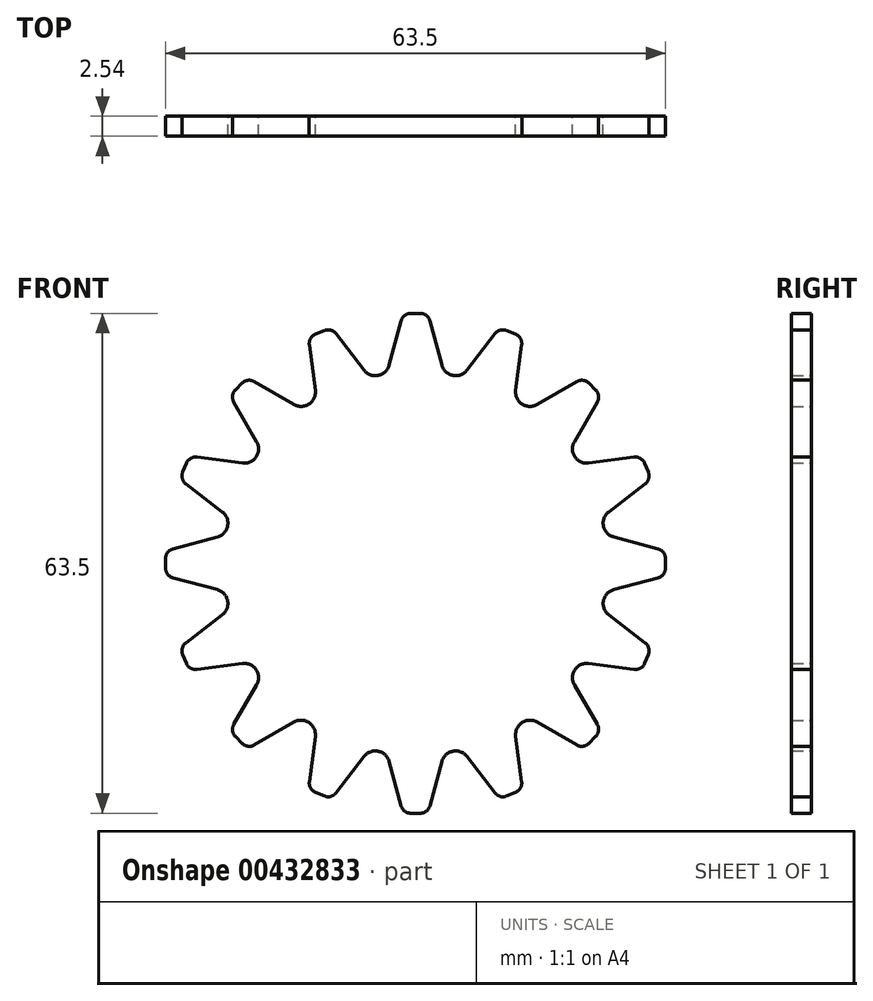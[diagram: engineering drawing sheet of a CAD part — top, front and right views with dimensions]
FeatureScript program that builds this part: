
annotation { "Feature Type Name" : "Feature", "Feature Type Description" : "" }
export const myFeature = defineFeature(function(context is Context, id is Id, definition is map)
    precondition{}
    {
        {
            var Q0;
            Q0=qCreatedBy(makeId("Front.planeOp"),FACE);
            var sketch = newSketch(context, id + "F0", { "sketchPlane" : qUnion([Q0])});
            skCircle(sketch, "E0", {"center": v(0, 0) * mm, "radius": 25.4 * mm, "construction": true});
            skPoint(sketch, "E1", {"position": v(0, 31.75) * mm});
            skLineSegment(sketch, "E2", {"start": v(-0.61, 31.75) * mm, "end": v(0.61, 31.75) * mm});
            skLineSegment(sketch, "E3", {"start": v(-1.84, 30.8) * mm, "end": v(-3.35, 25.18) * mm});
            skLineSegment(sketch, "E4.MirrorCS", {"start": v(1.84, 30.8) * mm, "end": v(3.35, 25.18) * mm});
            skPoint(sketch, "E5.visualSharp", {"position": v(-1.59, 31.75) * mm});
            skArc(sketch, "E5.filletArc", {"start": v(-0.61, 31.75) * mm, "mid": v(-1.39, 31.49) * mm, "end": v(-1.84, 30.8) * mm});
            skArc(sketch, "E6.MirrorCS", {"start": v(0.61, 31.75) * mm, "mid": v(1.39, 31.49) * mm, "end": v(1.84, 30.8) * mm});
            skPoint(sketch, "E7.orphan", {"position": v(1.59, 31.75) * mm});
            skArc(sketch, "E8", {"start": v(3.35, 25.18) * mm, "mid": v(4.75, 23.87) * mm, "end": v(6.54, 24.54) * mm});
            skLineSegment(sketch, "E9.1.0", {"start": v(-13.49, 27.76) * mm, "end": v(-12.73, 21.98) * mm});
            skArc(sketch, "E9.1.1", {"start": v(-12.72, 29.1) * mm, "mid": v(-13.33, 28.56) * mm, "end": v(-13.49, 27.76) * mm});
            skLineSegment(sketch, "E9.1.2", {"start": v(-12.72, 29.1) * mm, "end": v(-11.58, 29.57) * mm});
            skArc(sketch, "E9.1.3", {"start": v(-11.58, 29.57) * mm, "mid": v(-10.77, 29.62) * mm, "end": v(-10.1, 29.17) * mm});
            skLineSegment(sketch, "E9.1.4", {"start": v(-10.1, 29.17) * mm, "end": v(-6.54, 24.54) * mm});
            skArc(sketch, "E9.1.5", {"start": v(-6.54, 24.54) * mm, "mid": v(-4.75, 23.87) * mm, "end": v(-3.35, 25.18) * mm});
            skLineSegment(sketch, "E9.2.0", {"start": v(-23.09, 20.48) * mm, "end": v(-20.17, 15.44) * mm});
            skArc(sketch, "E9.2.1", {"start": v(-22.88, 22.02) * mm, "mid": v(-23.25, 21.28) * mm, "end": v(-23.09, 20.48) * mm});
            skLineSegment(sketch, "E9.2.2", {"start": v(-22.88, 22.02) * mm, "end": v(-22.02, 22.88) * mm});
            skArc(sketch, "E9.2.3", {"start": v(-22.02, 22.88) * mm, "mid": v(-21.28, 23.25) * mm, "end": v(-20.48, 23.09) * mm});
            skLineSegment(sketch, "E9.2.4", {"start": v(-20.48, 23.09) * mm, "end": v(-15.44, 20.17) * mm});
            skArc(sketch, "E9.2.5", {"start": v(-15.44, 20.17) * mm, "mid": v(-13.52, 20.23) * mm, "end": v(-12.73, 21.98) * mm});
            skLineSegment(sketch, "E9.3.0", {"start": v(-29.17, 10.1) * mm, "end": v(-24.54, 6.54) * mm});
            skArc(sketch, "E9.3.1", {"start": v(-29.57, 11.58) * mm, "mid": v(-29.62, 10.77) * mm, "end": v(-29.17, 10.1) * mm});
            skLineSegment(sketch, "E9.3.2", {"start": v(-29.57, 11.58) * mm, "end": v(-29.1, 12.72) * mm});
            skArc(sketch, "E9.3.3", {"start": v(-29.1, 12.72) * mm, "mid": v(-28.56, 13.33) * mm, "end": v(-27.76, 13.49) * mm});
            skLineSegment(sketch, "E9.3.4", {"start": v(-27.76, 13.49) * mm, "end": v(-21.98, 12.73) * mm});
            skArc(sketch, "E9.3.5", {"start": v(-21.98, 12.73) * mm, "mid": v(-20.23, 13.52) * mm, "end": v(-20.17, 15.44) * mm});
            skLineSegment(sketch, "E9.4.0", {"start": v(-30.8, -1.84) * mm, "end": v(-25.18, -3.35) * mm});
            skArc(sketch, "E9.4.1", {"start": v(-31.75, -0.61) * mm, "mid": v(-31.49, -1.39) * mm, "end": v(-30.8, -1.84) * mm});
            skLineSegment(sketch, "E9.4.2", {"start": v(-31.75, -0.61) * mm, "end": v(-31.75, 0.61) * mm});
            skArc(sketch, "E9.4.3", {"start": v(-31.75, 0.61) * mm, "mid": v(-31.49, 1.39) * mm, "end": v(-30.8, 1.84) * mm});
            skLineSegment(sketch, "E9.4.4", {"start": v(-30.8, 1.84) * mm, "end": v(-25.18, 3.35) * mm});
            skArc(sketch, "E9.4.5", {"start": v(-25.18, 3.35) * mm, "mid": v(-23.87, 4.75) * mm, "end": v(-24.54, 6.54) * mm});
            skLineSegment(sketch, "E9.5.0", {"start": v(-27.76, -13.49) * mm, "end": v(-21.98, -12.73) * mm});
            skArc(sketch, "E9.5.1", {"start": v(-29.1, -12.72) * mm, "mid": v(-28.56, -13.33) * mm, "end": v(-27.76, -13.49) * mm});
            skLineSegment(sketch, "E9.5.2", {"start": v(-29.1, -12.72) * mm, "end": v(-29.57, -11.58) * mm});
            skArc(sketch, "E9.5.3", {"start": v(-29.57, -11.58) * mm, "mid": v(-29.62, -10.77) * mm, "end": v(-29.17, -10.1) * mm});
            skLineSegment(sketch, "E9.5.4", {"start": v(-29.17, -10.1) * mm, "end": v(-24.54, -6.54) * mm});
            skArc(sketch, "E9.5.5", {"start": v(-24.54, -6.54) * mm, "mid": v(-23.87, -4.75) * mm, "end": v(-25.18, -3.35) * mm});
            skLineSegment(sketch, "E9.6.0", {"start": v(-20.48, -23.09) * mm, "end": v(-15.44, -20.17) * mm});
            skArc(sketch, "E9.6.1", {"start": v(-22.02, -22.88) * mm, "mid": v(-21.28, -23.25) * mm, "end": v(-20.48, -23.09) * mm});
            skLineSegment(sketch, "E9.6.2", {"start": v(-22.02, -22.88) * mm, "end": v(-22.88, -22.02) * mm});
            skArc(sketch, "E9.6.3", {"start": v(-22.88, -22.02) * mm, "mid": v(-23.25, -21.28) * mm, "end": v(-23.09, -20.48) * mm});
            skLineSegment(sketch, "E9.6.4", {"start": v(-23.09, -20.48) * mm, "end": v(-20.17, -15.44) * mm});
            skArc(sketch, "E9.6.5", {"start": v(-20.17, -15.44) * mm, "mid": v(-20.23, -13.52) * mm, "end": v(-21.98, -12.73) * mm});
            skLineSegment(sketch, "E9.7.0", {"start": v(-10.1, -29.17) * mm, "end": v(-6.54, -24.54) * mm});
            skArc(sketch, "E9.7.1", {"start": v(-11.58, -29.57) * mm, "mid": v(-10.77, -29.62) * mm, "end": v(-10.1, -29.17) * mm});
            skLineSegment(sketch, "E9.7.2", {"start": v(-11.58, -29.57) * mm, "end": v(-12.72, -29.1) * mm});
            skArc(sketch, "E9.7.3", {"start": v(-12.72, -29.1) * mm, "mid": v(-13.33, -28.56) * mm, "end": v(-13.49, -27.76) * mm});
            skLineSegment(sketch, "E9.7.4", {"start": v(-13.49, -27.76) * mm, "end": v(-12.73, -21.98) * mm});
            skArc(sketch, "E9.7.5", {"start": v(-12.73, -21.98) * mm, "mid": v(-13.52, -20.23) * mm, "end": v(-15.44, -20.17) * mm});
            skLineSegment(sketch, "E9.8.0", {"start": v(1.84, -30.8) * mm, "end": v(3.35, -25.18) * mm});
            skArc(sketch, "E9.8.1", {"start": v(0.61, -31.75) * mm, "mid": v(1.39, -31.49) * mm, "end": v(1.84, -30.8) * mm});
            skLineSegment(sketch, "E9.8.2", {"start": v(0.61, -31.75) * mm, "end": v(-0.61, -31.75) * mm});
            skArc(sketch, "E9.8.3", {"start": v(-0.61, -31.75) * mm, "mid": v(-1.39, -31.49) * mm, "end": v(-1.84, -30.8) * mm});
            skLineSegment(sketch, "E9.8.4", {"start": v(-1.84, -30.8) * mm, "end": v(-3.35, -25.18) * mm});
            skArc(sketch, "E9.8.5", {"start": v(-3.35, -25.18) * mm, "mid": v(-4.75, -23.87) * mm, "end": v(-6.54, -24.54) * mm});
            skLineSegment(sketch, "E9.9.0", {"start": v(13.49, -27.76) * mm, "end": v(12.73, -21.98) * mm});
            skArc(sketch, "E9.9.1", {"start": v(12.72, -29.1) * mm, "mid": v(13.33, -28.56) * mm, "end": v(13.49, -27.76) * mm});
            skLineSegment(sketch, "E9.9.2", {"start": v(12.72, -29.1) * mm, "end": v(11.58, -29.57) * mm});
            skArc(sketch, "E9.9.3", {"start": v(11.58, -29.57) * mm, "mid": v(10.77, -29.62) * mm, "end": v(10.1, -29.17) * mm});
            skLineSegment(sketch, "E9.9.4", {"start": v(10.1, -29.17) * mm, "end": v(6.54, -24.54) * mm});
            skArc(sketch, "E9.9.5", {"start": v(6.54, -24.54) * mm, "mid": v(4.75, -23.87) * mm, "end": v(3.35, -25.18) * mm});
            skLineSegment(sketch, "E9.10.0", {"start": v(23.09, -20.48) * mm, "end": v(20.17, -15.44) * mm});
            skArc(sketch, "E9.10.1", {"start": v(22.88, -22.02) * mm, "mid": v(23.25, -21.28) * mm, "end": v(23.09, -20.48) * mm});
            skLineSegment(sketch, "E9.10.2", {"start": v(22.88, -22.02) * mm, "end": v(22.02, -22.88) * mm});
            skArc(sketch, "E9.10.3", {"start": v(22.02, -22.88) * mm, "mid": v(21.28, -23.25) * mm, "end": v(20.48, -23.09) * mm});
            skLineSegment(sketch, "E9.10.4", {"start": v(20.48, -23.09) * mm, "end": v(15.44, -20.17) * mm});
            skArc(sketch, "E9.10.5", {"start": v(15.44, -20.17) * mm, "mid": v(13.52, -20.23) * mm, "end": v(12.73, -21.98) * mm});
            skLineSegment(sketch, "E9.11.0", {"start": v(29.17, -10.1) * mm, "end": v(24.54, -6.54) * mm});
            skArc(sketch, "E9.11.1", {"start": v(29.57, -11.58) * mm, "mid": v(29.62, -10.77) * mm, "end": v(29.17, -10.1) * mm});
            skLineSegment(sketch, "E9.11.2", {"start": v(29.57, -11.58) * mm, "end": v(29.1, -12.72) * mm});
            skArc(sketch, "E9.11.3", {"start": v(29.1, -12.72) * mm, "mid": v(28.56, -13.33) * mm, "end": v(27.76, -13.49) * mm});
            skLineSegment(sketch, "E9.11.4", {"start": v(27.76, -13.49) * mm, "end": v(21.98, -12.73) * mm});
            skArc(sketch, "E9.11.5", {"start": v(21.98, -12.73) * mm, "mid": v(20.23, -13.52) * mm, "end": v(20.17, -15.44) * mm});
            skLineSegment(sketch, "E9.12.0", {"start": v(30.8, 1.84) * mm, "end": v(25.18, 3.35) * mm});
            skArc(sketch, "E9.12.1", {"start": v(31.75, 0.61) * mm, "mid": v(31.49, 1.39) * mm, "end": v(30.8, 1.84) * mm});
            skLineSegment(sketch, "E9.12.2", {"start": v(31.75, 0.61) * mm, "end": v(31.75, -0.61) * mm});
            skArc(sketch, "E9.12.3", {"start": v(31.75, -0.61) * mm, "mid": v(31.49, -1.39) * mm, "end": v(30.8, -1.84) * mm});
            skLineSegment(sketch, "E9.12.4", {"start": v(30.8, -1.84) * mm, "end": v(25.18, -3.35) * mm});
            skArc(sketch, "E9.12.5", {"start": v(25.18, -3.35) * mm, "mid": v(23.87, -4.75) * mm, "end": v(24.54, -6.54) * mm});
            skLineSegment(sketch, "E9.13.0", {"start": v(27.76, 13.49) * mm, "end": v(21.98, 12.73) * mm});
            skArc(sketch, "E9.13.1", {"start": v(29.1, 12.72) * mm, "mid": v(28.56, 13.33) * mm, "end": v(27.76, 13.49) * mm});
            skLineSegment(sketch, "E9.13.2", {"start": v(29.1, 12.72) * mm, "end": v(29.57, 11.58) * mm});
            skArc(sketch, "E9.13.3", {"start": v(29.57, 11.58) * mm, "mid": v(29.62, 10.77) * mm, "end": v(29.17, 10.1) * mm});
            skLineSegment(sketch, "E9.13.4", {"start": v(29.17, 10.1) * mm, "end": v(24.54, 6.54) * mm});
            skArc(sketch, "E9.13.5", {"start": v(24.54, 6.54) * mm, "mid": v(23.87, 4.75) * mm, "end": v(25.18, 3.35) * mm});
            skLineSegment(sketch, "E9.14.0", {"start": v(20.48, 23.09) * mm, "end": v(15.44, 20.17) * mm});
            skArc(sketch, "E9.14.1", {"start": v(22.02, 22.88) * mm, "mid": v(21.28, 23.25) * mm, "end": v(20.48, 23.09) * mm});
            skLineSegment(sketch, "E9.14.2", {"start": v(22.02, 22.88) * mm, "end": v(22.88, 22.02) * mm});
            skArc(sketch, "E9.14.3", {"start": v(22.88, 22.02) * mm, "mid": v(23.25, 21.28) * mm, "end": v(23.09, 20.48) * mm});
            skLineSegment(sketch, "E9.14.4", {"start": v(23.09, 20.48) * mm, "end": v(20.17, 15.44) * mm});
            skArc(sketch, "E9.14.5", {"start": v(20.17, 15.44) * mm, "mid": v(20.23, 13.52) * mm, "end": v(21.98, 12.73) * mm});
            skLineSegment(sketch, "E9.15.0", {"start": v(10.1, 29.17) * mm, "end": v(6.54, 24.54) * mm});
            skArc(sketch, "E9.15.1", {"start": v(11.58, 29.57) * mm, "mid": v(10.77, 29.62) * mm, "end": v(10.1, 29.17) * mm});
            skLineSegment(sketch, "E9.15.2", {"start": v(11.58, 29.57) * mm, "end": v(12.72, 29.1) * mm});
            skArc(sketch, "E9.15.3", {"start": v(12.72, 29.1) * mm, "mid": v(13.33, 28.56) * mm, "end": v(13.49, 27.76) * mm});
            skLineSegment(sketch, "E9.15.4", {"start": v(13.49, 27.76) * mm, "end": v(12.73, 21.98) * mm});
            skArc(sketch, "E9.15.5", {"start": v(12.73, 21.98) * mm, "mid": v(13.52, 20.23) * mm, "end": v(15.44, 20.17) * mm});
            skSolve(sketch);
        }
        {
            var Q0;
            Q0 = qSketchRegion(id + "F0", true);
            extrude(context, id + "F1", {"entities" : qUnion([Q0]), "depth" : 2.54 * mm});
        }
    });
